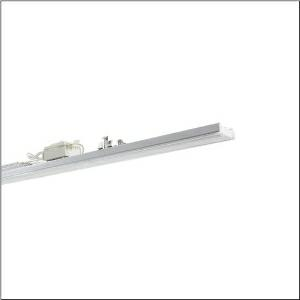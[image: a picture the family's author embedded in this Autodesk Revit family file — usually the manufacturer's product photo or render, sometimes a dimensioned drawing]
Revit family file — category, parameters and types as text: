
# Revit family: licross_r__21_recessed_mo_52tl12mn4a5g_9149
name_source: partatom
category: Lighting Fixtures
units: mm (PartAtom-declared; Revit-internal decimal feet)

## family parameters
Cut with Voids When Loaded = No
Host = Face
Light Source = No
Part Type = Normal
Room Calculation Point = No
Round Connector Dimension = Use Diameter
Shared = No

## types (1)
- --- (1 x LED, 10990 lm, 60.5 W, 4000K)
    Apparent Load = 61 VA
    CIE Flux Codes = 72 92 99 100 100
    Color Rendering = 80
    Color Temperature = 4000K
    Default Elevation = 1800 mm
    Description = Licross® 21 Recessed MO, luminaire insert, of sheet steel, galvanised, coil coated, white, length: 1.500mm, width: 66mm, height: 67mm, LED rated luminous flux: 10.990lm, light colour: 840, control gear: ON/OFF Multilumen, with plug, 3-pole, with phase selection, mains connection: 220..240V, AC, 50/60Hz, rated input power: 61W, internal wiring halogen-free, primary optical cover: cover, of PMMA, light emission: direct distribution, primary light characteristic: symmetric, protection rating (complete): IP40, insulation class (complete): insulation class I (protective earthing), certification: CE, ENEC, VDE, UKCA, protection symbol: D if used in an environment without relevant dust loads with corresponding accessories, impact resistance: IK06, permissible ambient temperature for indoor applications: -35..+40°C, corresponds to IFS (International Featured Standards) requirements for safety and quality in the food industry, reducing of maximum allowable ambient temperature of 5°C with ceiling mounting, LABS conformity tested according to VDMA 24364:2018-05, packaging unit: 1 piece
    Height = 58 mm
    Lamp = 1 x LED
    Lamp Light Flux = 10990 lm
    Lamp Power = 60.5 W
    Lamp count = 1
    Length = 1500 mm
    Luminous efficacy = 182 lm/W
    Manufacturer = Siteco
    ModVariant = No
    Model = 52TL12MN4A5G
    Mounting Place = Ceiling
    Mounting Type = Pendant
    Number of Poles = 1
    OnlyDefault = Yes
    Power Factor = 1
    Product Name = Licross® 21 Recessed MO
    Product group = luminaire insert | ceiling pendant
    ProductGroupID = 902
    Protection Class = Protection class I
    Protection Degree = IP 40
    RLX_Detail_Level = 1
    RLX_Emergency_Light_Flux = 0 lm
    RLX_Emergency_Type = 0
    RLX_Emergency_Type_DB = No
    RlxData = <blob elided: 22321 chars, md5=b5ae4627>
    Socket = socket
    Standby Power = 0 W
    System Light Flux = 10990 lm
    System Power = 61 W
    Type Comments = factory setting: luminous flux: 100 % | (A | C | E) | 140 mA
    Type Image = l_1296930.jpg
    URL = http://relux.com
    VarID = @adj_129451
    Voltage = 0 V
    Weight = 0.00 kg
    Width = 66 mm

## geometry (parser evidence)
native form markers: Blend x4, Sweep x13
no freeform markers — native parametric forms only
